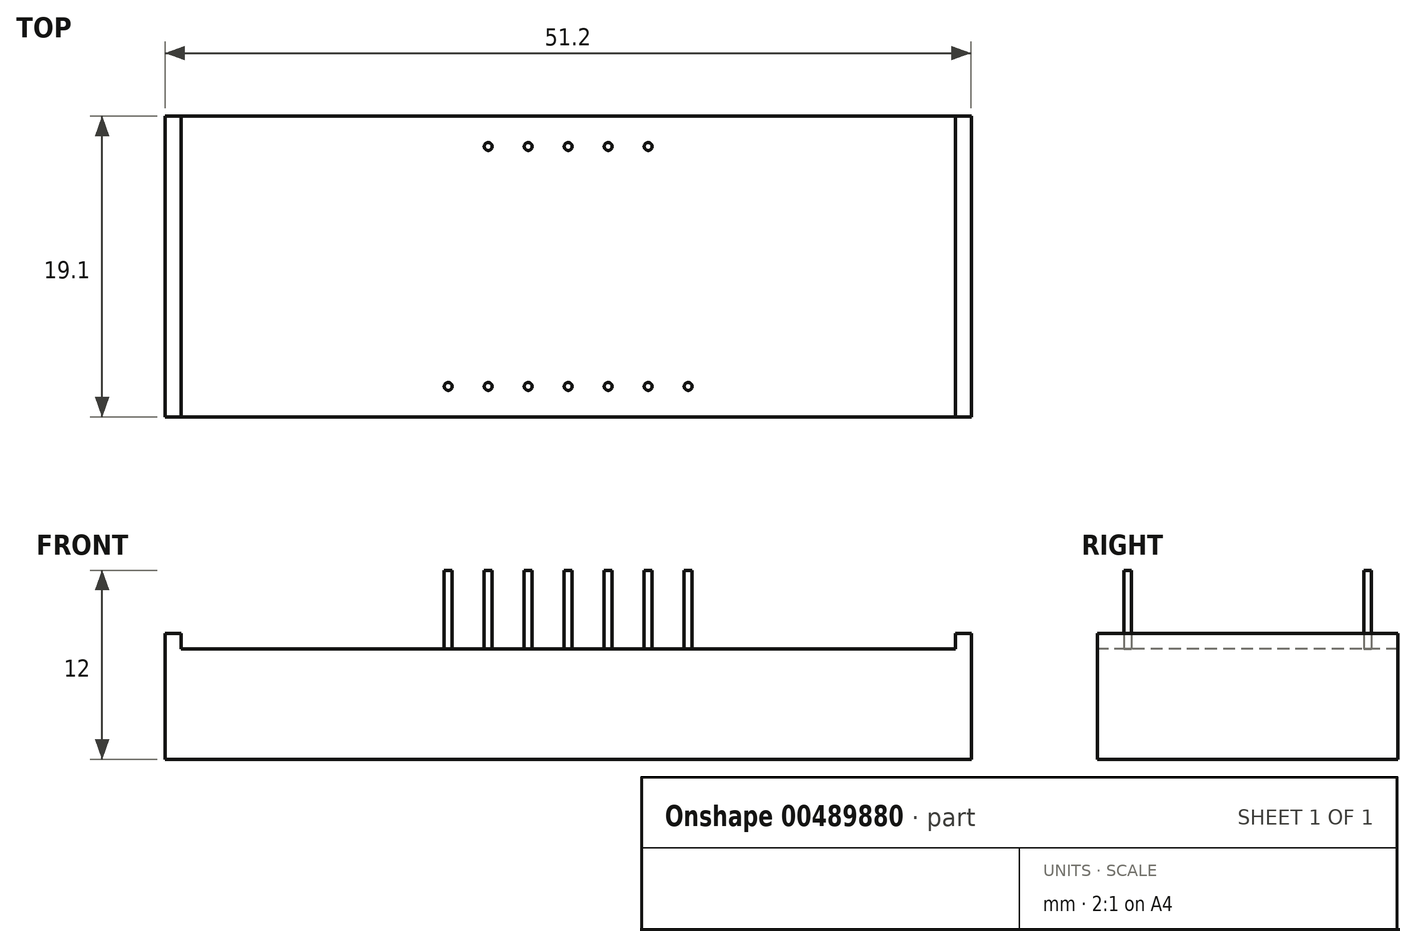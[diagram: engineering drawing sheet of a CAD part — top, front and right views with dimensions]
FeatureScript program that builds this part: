
annotation { "Feature Type Name" : "Feature", "Feature Type Description" : "" }
export const myFeature = defineFeature(function(context is Context, id is Id, definition is map)
    precondition{}
    {
        {
            var Q0;
            Q0=qCreatedBy(makeId("Top.planeOp"),FACE);
            var sketch = newSketch(context, id + "F0", { "sketchPlane" : qUnion([Q0])});
            skLineSegment(sketch, "E0.bottom", {"start": v(-40.76, -13.08) * mm, "end": v(10.44, -13.08) * mm});
            skLineSegment(sketch, "E0.top", {"start": v(-40.76, -32.18) * mm, "end": v(10.44, -32.18) * mm});
            skLineSegment(sketch, "E0.left", {"start": v(-40.76, -13.08) * mm, "end": v(-40.76, -32.18) * mm});
            skLineSegment(sketch, "E1", {"start": v(10.44, -13.08) * mm, "end": v(10.44, -32.18) * mm});
            skSolve(sketch);
        }
        {
            var Q0;
            Q0 = qSketchRegion(id + "F0", true);
            extrude(context, id + "F1", {"entities" : qUnion([Q0]), "depth" : 7 * mm});
        }
        {
            var Q0;
            Q0=makeQuery(id+"F1.opExtrude","CAP_FACE",FACE,{"disambiguationData":[OSD([sQuery(id+"F0.wireOp",EDGE,"E0.bottom"),sQuery(id+"F0.wireOp",EDGE,"E0.top"),sQuery(id+"F0.wireOp",EDGE,"E0.left"),sQuery(id+"F0.wireOp",EDGE,"E1")])],"isStart":false});
            var sketch = newSketch(context, id + "F2", { "sketchPlane" : qUnion([Q0])});
            skSolve(sketch);
        }
        {
            var Q0;
            Q0=makeQuery(id+"F2.imprint","IMPRINT",FACE,{"disambiguationData":[TD([[makeQuery(id+"F2.imprint","IMPRINT",EDGE,{"derivedFrom":makeQuery(id+"F1.opExtrude","CAP_EDGE",EDGE,{"disambiguationData":[OSD([sQuery(id+"F0.wireOp",EDGE,"E0.bottom")])],"isStart":false})}),-1.0]])]});
            var sketch = newSketch(context, id + "F3", { "sketchPlane" : qUnion([Q0])});
            skLineSegment(sketch, "E2.bottom", {"start": v(-40.76, -13.08) * mm, "end": v(-39.76, -13.08) * mm});
            skLineSegment(sketch, "E2.top", {"start": v(-40.76, -32.18) * mm, "end": v(-39.76, -32.18) * mm});
            skLineSegment(sketch, "E2.left", {"start": v(-40.76, -13.08) * mm, "end": v(-40.76, -32.18) * mm});
            skLineSegment(sketch, "E2.right", {"start": v(-39.76, -13.08) * mm, "end": v(-39.76, -32.18) * mm});
            skSolve(sketch);
        }
        {
            var Q0;
            Q0 = qSketchRegion(id + "F3", true);
            extrude(context, id + "F4", {"entities" : qUnion([Q0]), "operationType" : NewBodyOperationType.ADD, "depth" : 1 * mm});
        }
        {
            var Q0;
            Q0=makeQuery(id+"F2.imprint","IMPRINT",FACE,{"disambiguationData":[TD([[makeQuery(id+"F2.imprint","IMPRINT",EDGE,{"derivedFrom":makeQuery(id+"F1.opExtrude","CAP_EDGE",EDGE,{"disambiguationData":[OSD([sQuery(id+"F0.wireOp",EDGE,"E0.bottom")])],"isStart":false})}),-1.0]])]});
            var sketch = newSketch(context, id + "F5", { "sketchPlane" : qUnion([Q0])});
            skLineSegment(sketch, "E3.bottom", {"start": v(9.44, -13.08) * mm, "end": v(10.44, -13.08) * mm});
            skLineSegment(sketch, "E3.top", {"start": v(9.44, -32.18) * mm, "end": v(10.44, -32.18) * mm});
            skLineSegment(sketch, "E3.left", {"start": v(9.44, -13.08) * mm, "end": v(9.44, -32.18) * mm});
            skLineSegment(sketch, "E3.right", {"start": v(10.44, -13.08) * mm, "end": v(10.44, -32.18) * mm});
            skSolve(sketch);
        }
        {
            var Q0;
            Q0 = qSketchRegion(id + "F5", true);
            extrude(context, id + "F6", {"entities" : qUnion([Q0]), "operationType" : NewBodyOperationType.ADD, "depth" : 1 * mm});
        }
        {
            var Q0;
            Q0=makeQuery(id+"F2.imprint","IMPRINT",FACE,{"disambiguationData":[TD([[makeQuery(id+"F2.imprint","IMPRINT",EDGE,{"derivedFrom":makeQuery(id+"F1.opExtrude","CAP_EDGE",EDGE,{"disambiguationData":[OSD([sQuery(id+"F0.wireOp",EDGE,"E0.bottom")])],"isStart":false})}),-1.0]])]});
            var sketch = newSketch(context, id + "F7", { "sketchPlane" : qUnion([Q0])});
            skCircle(sketch, "E4", {"center": v(-15.16, -15) * mm, "radius": 0.25 * mm});
            skCircle(sketch, "E5", {"center": v(-15.16, -30.25) * mm, "radius": 0.25 * mm});
            skCircle(sketch, "E6.1.0.0", {"center": v(-12.62, -15) * mm, "radius": 0.25 * mm});
            skCircle(sketch, "E6.2.0.0", {"center": v(-10.08, -15) * mm, "radius": 0.25 * mm});
            skLineSegment(sketch, "E6.direction1", {"start": v(-15.16, -15) * mm, "end": v(-12.62, -15) * mm, "construction": true});
            skCircle(sketch, "E7.1.0.0", {"center": v(-17.7, -15) * mm, "radius": 0.25 * mm});
            skCircle(sketch, "E7.2.0.0", {"center": v(-20.24, -15) * mm, "radius": 0.25 * mm});
            skLineSegment(sketch, "E7.direction1", {"start": v(-15.16, -15) * mm, "end": v(-17.7, -15) * mm, "construction": true});
            skCircle(sketch, "E8.1.0.0", {"center": v(-12.62, -30.25) * mm, "radius": 0.25 * mm});
            skCircle(sketch, "E8.2.0.0", {"center": v(-10.08, -30.25) * mm, "radius": 0.25 * mm});
            skLineSegment(sketch, "E8.direction1", {"start": v(-15.16, -30.25) * mm, "end": v(-12.62, -30.25) * mm, "construction": true});
            skCircle(sketch, "E9.0.3.0", {"center": v(-7.54, -30.25) * mm, "radius": 0.25 * mm});
            skCircle(sketch, "E10.1.0.0", {"center": v(-17.7, -30.25) * mm, "radius": 0.25 * mm});
            skCircle(sketch, "E10.2.0.0", {"center": v(-20.24, -30.25) * mm, "radius": 0.25 * mm});
            skLineSegment(sketch, "E10.direction1", {"start": v(-15.16, -30.25) * mm, "end": v(-17.7, -30.25) * mm, "construction": true});
            skCircle(sketch, "E11.0.3.0", {"center": v(-22.78, -30.25) * mm, "radius": 0.25 * mm});
            skSolve(sketch);
        }
        {
            var Q0;
            Q0 = qSketchRegion(id + "F7", true);
            extrude(context, id + "F8", {"entities" : qUnion([Q0]), "operationType" : NewBodyOperationType.ADD, "depth" : 5 * mm});
        }
    });
